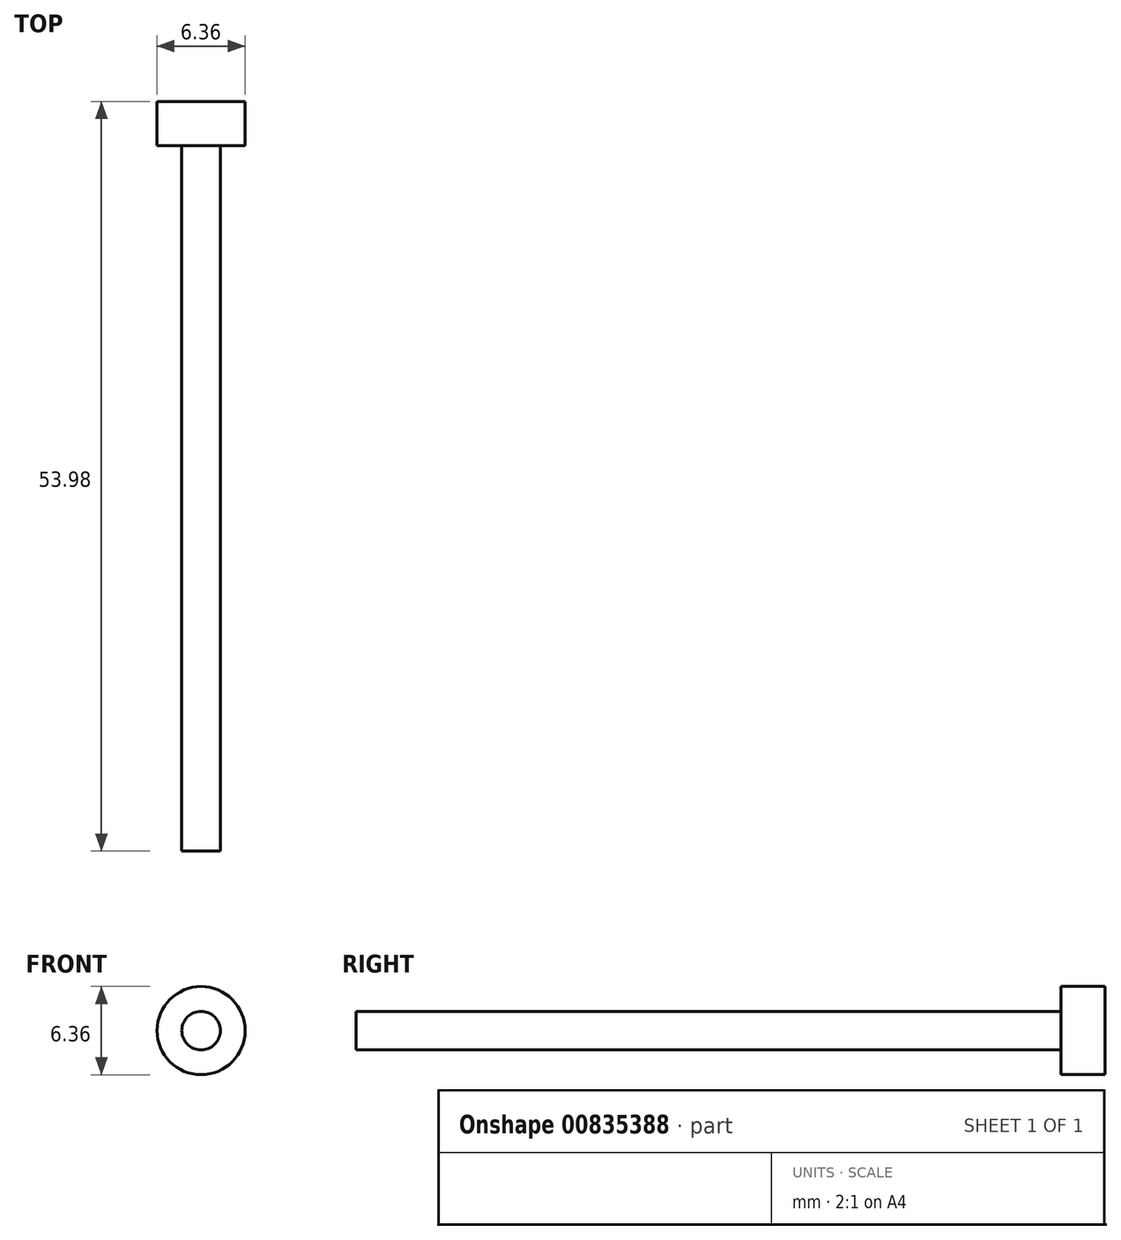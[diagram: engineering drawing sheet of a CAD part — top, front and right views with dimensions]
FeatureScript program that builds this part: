
annotation { "Feature Type Name" : "Feature", "Feature Type Description" : "" }
export const myFeature = defineFeature(function(context is Context, id is Id, definition is map)
    precondition{}
    {
        {
            var Q0;
            Q0=qCreatedBy(makeId("Front.planeOp"),FACE);
            var sketch = newSketch(context, id + "F0", { "sketchPlane" : qUnion([Q0])});
            skCircle(sketch, "E0", {"center": v(0, 0) * mm, "radius": 1.39 * mm});
            skSolve(sketch);
        }
        {
            var Q0;
            Q0=makeQuery(id+"F0.imprint","IMPRINT",FACE,{"disambiguationData":[TD([[makeQuery(id+"F0.imprint","IMPRINT",EDGE,{"derivedFrom":sQuery(id+"F0.wireOp",EDGE,"E0")}),1.0]])]});
            var Q1;
            {var subQ1=sQuery(id+"F0.wireOp",EDGE,"vR2S5VTx-2Lfx-I2jy-zZPw-cHreWlS8JblK.bottom");Q1=makeQuery(id+"F0.imprint","IMPRINT",FACE,{"disambiguationData":[TD([[makeQuery(id+"F0.imprint","IMPRINT",EDGE,{"derivedFrom":subQ1}),-1.0]])]});}
            extrude(context, id + "F1", {"entities" : qUnion([Q0, Q1]), "depth" : 50.8 * mm, "offsetDistance" : 25.4 * mm});
        }
        {
            var Q0;
            Q0=qCreatedBy(makeId("Front.planeOp"),FACE);
            var sketch = newSketch(context, id + "F2", { "sketchPlane" : qUnion([Q0])});
            skCircle(sketch, "E1", {"center": v(0, 0) * mm, "radius": 3.18 * mm});
            skSolve(sketch);
        }
        {
            var Q0;
            Q0=makeQuery(id+"F2.imprint","IMPRINT",FACE,{"disambiguationData":[TD([[makeQuery(id+"F2.imprint","IMPRINT",EDGE,{"derivedFrom":sQuery(id+"F2.wireOp",EDGE,"E1")}),1.0]])]});
            extrude(context, id + "F3", {"entities" : qUnion([Q0]), "operationType" : NewBodyOperationType.ADD, "oppositeDirection" : true, "depth" : 3.17 * mm, "offsetDistance" : 25.4 * mm});
        }
    });
